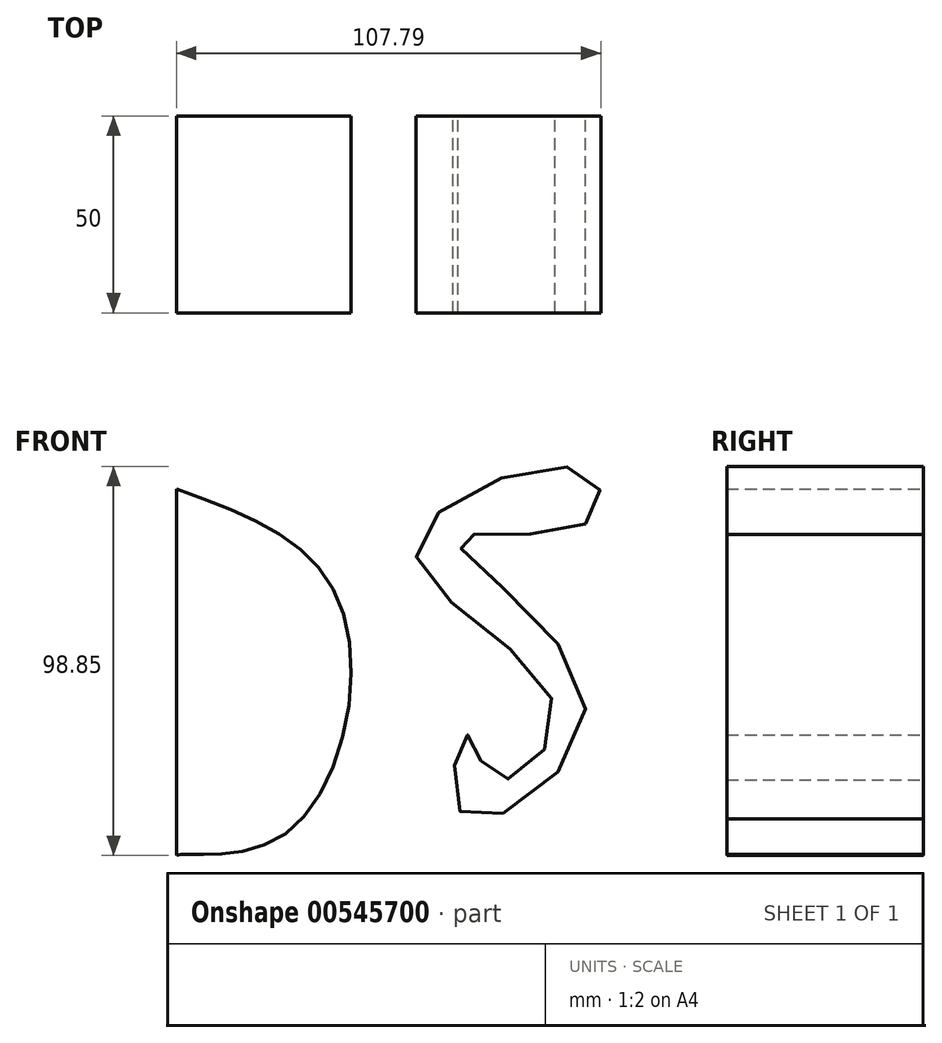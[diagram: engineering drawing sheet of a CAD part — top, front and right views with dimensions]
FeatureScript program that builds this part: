
annotation { "Feature Type Name" : "Feature", "Feature Type Description" : "" }
export const myFeature = defineFeature(function(context is Context, id is Id, definition is map)
    precondition{}
    {
        {
            var Q0;
            Q0=qCreatedBy(makeId("Front.planeOp"),FACE);
            var sketch = newSketch(context, id + "F0", { "sketchPlane" : qUnion([Q0])});
            skLineSegment(sketch, "E0", {"start": v(-58.58, 47.25) * mm, "end": v(-58.58, -45.87) * mm});
            skFitSpline(sketch, "E1", {"points": [v(-58.58, 47.25) * mm, v(-17.13, 18.24) * mm, v(-29.84, -39.51) * mm, v(-56.1, -45.6) * mm, v(-58.58, -45.87) * mm], "startDerivative": vector(159.37, -57.68) * mm, "endDerivative": vector(-23.46, -5.37) * mm});
            skFitSpline(sketch, "E2", {"points": [v(45.32, 38.4) * mm, v(12.99, 34.26) * mm, v(45.32, -7.74) * mm, v(14.1, -35.37) * mm, v(15.2, -15.2) * mm, v(22.38, -26.25) * mm, v(37.3, -8.01) * mm, v(2.21, 32.05) * mm, v(44.49, 51.95) * mm, v(45.32, 38.4) * mm]});
            skLineSegment(sketch, "E3", {"start": v(-43.93, 12.16) * mm, "end": v(-43.93, -9.67) * mm, "construction": true});
            skSolve(sketch);
        }
        {
            var Q0;
            Q0 = qSketchRegion(id + "F0", true);
            extrude(context, id + "F1", {"entities" : qUnion([Q0]), "depth" : 50 * mm, "offsetDistance" : 25 * mm});
        }
    });
